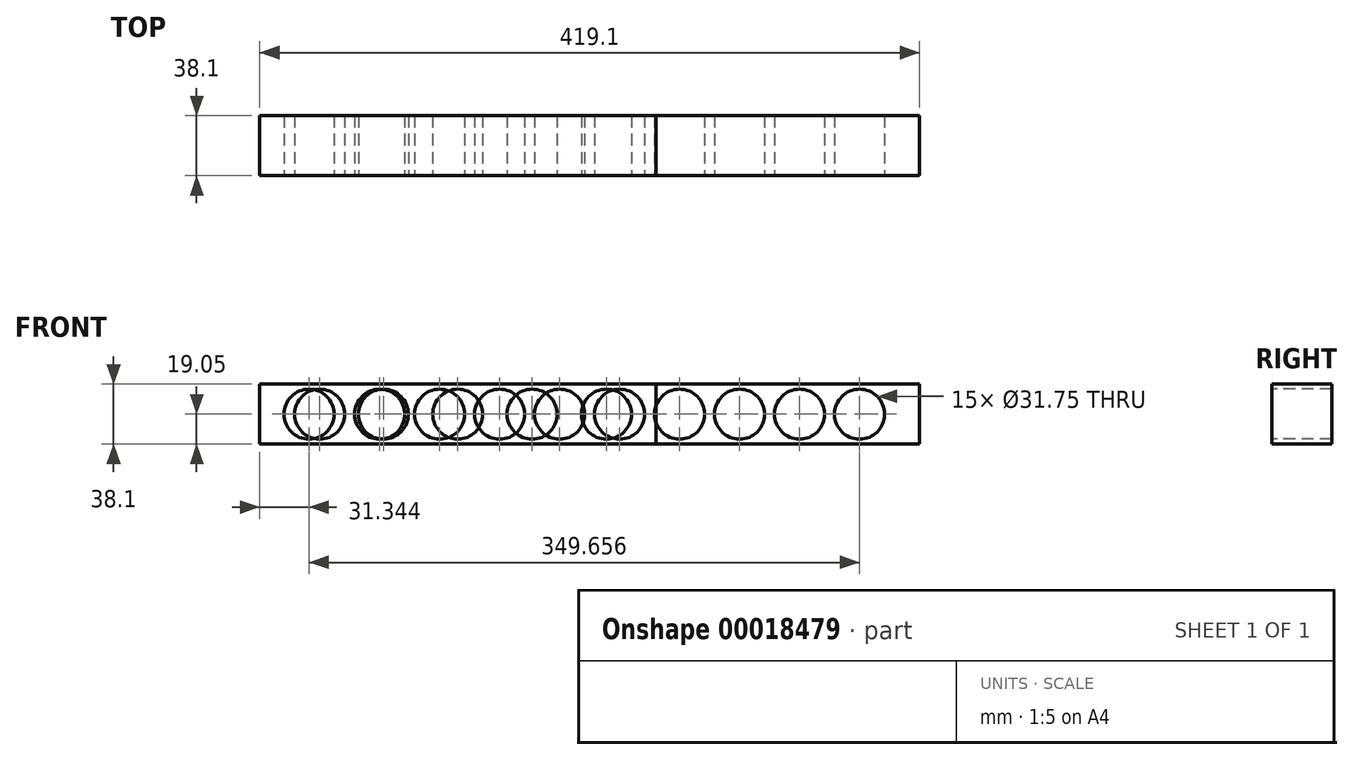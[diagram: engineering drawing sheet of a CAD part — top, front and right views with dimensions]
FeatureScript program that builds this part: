
annotation { "Feature Type Name" : "Feature", "Feature Type Description" : "" }
export const myFeature = defineFeature(function(context is Context, id is Id, definition is map)
    precondition{}
    {
        {
            var Q0;
            Q0=qCreatedBy(makeId("Right.planeOp"),FACE);
            var sketch = newSketch(context, id + "F0", { "sketchPlane" : qUnion([Q0])});
            skLineSegment(sketch, "E0.bottom", {"start": v(0, 0) * mm, "end": v(38.1, 0) * mm});
            skLineSegment(sketch, "E0.top", {"start": v(0, 38.1) * mm, "end": v(38.1, 38.1) * mm});
            skLineSegment(sketch, "E0.left", {"start": v(0, 0) * mm, "end": v(0, 38.1) * mm});
            skLineSegment(sketch, "E0.right", {"start": v(38.1, 0) * mm, "end": v(38.1, 38.1) * mm});
            skSolve(sketch);
        }
        {
            var Q0;
            Q0=makeQuery(id+"F0.imprint","IMPRINT",FACE,{"disambiguationData":[TD([[makeQuery(id+"F0.imprint","IMPRINT",EDGE,{"derivedFrom":sQuery(id+"F0.wireOp",EDGE,"E0.bottom")}),1.0]])]});
            extrude(context, id + "F1", {"entities" : qUnion([Q0]), "depth" : 419.1 * mm});
        }
        {
            var Q0;
            Q0=makeQuery(id+"F1.opExtrude","SWEPT_FACE",FACE,{"disambiguationData":[OSD([sQuery(id+"F0.wireOp",EDGE,"E0.left")])]});
            var sketch = newSketch(context, id + "F2", { "sketchPlane" : qUnion([Q0])});
            skPoint(sketch, "E1", {"position": v(38.1, 19.05) * mm});
            skPoint(sketch, "E2.1.0.0", {"position": v(76.2, 19.05) * mm});
            skPoint(sketch, "E2.2.0.0", {"position": v(114.3, 19.05) * mm});
            skPoint(sketch, "E2.3.0.0", {"position": v(152.4, 19.05) * mm});
            skPoint(sketch, "E2.4.0.0", {"position": v(190.5, 19.05) * mm});
            skPoint(sketch, "E2.5.0.0", {"position": v(228.6, 19.05) * mm});
            skPoint(sketch, "E2.6.0.0", {"position": v(266.7, 19.05) * mm});
            skPoint(sketch, "E2.7.0.0", {"position": v(304.8, 19.05) * mm});
            skPoint(sketch, "E2.8.0.0", {"position": v(342.9, 19.05) * mm});
            skPoint(sketch, "E2.9.0.0", {"position": v(381, 19.05) * mm});
            skLineSegment(sketch, "E2.direction1", {"start": v(38.1, 19.05) * mm, "end": v(76.2, 19.05) * mm, "construction": true});
            skSolve(sketch);
        }
        {
            var Q0;
            Q0=sQuery(id+"F2.wireOp",VERTEX,"E1");
            var Q1;
            Q1=sQuery(id+"F2.wireOp",VERTEX,"E2.1.0.0");
            var Q2;
            Q2=sQuery(id+"F2.wireOp",VERTEX,"E2.2.0.0");
            var Q3;
            Q3=sQuery(id+"F2.wireOp",VERTEX,"E2.3.0.0");
            var Q4;
            Q4=sQuery(id+"F2.wireOp",VERTEX,"E2.4.0.0");
            var Q5;
            Q5=sQuery(id+"F2.wireOp",VERTEX,"E2.5.0.0");
            var Q6;
            Q6=sQuery(id+"F2.wireOp",VERTEX,"E2.6.0.0");
            var Q7;
            Q7=sQuery(id+"F2.wireOp",VERTEX,"E2.7.0.0");
            var Q8;
            Q8=sQuery(id+"F2.wireOp",VERTEX,"E2.8.0.0");
            var Q9;
            Q9=sQuery(id+"F2.wireOp",VERTEX,"E2.9.0.0");
            var Q10;
            Q10=makeQuery(id+"F1.opExtrude","SWEPT_BODY",BODY,{"disambiguationData":[OSD([sQuery(id+"F0.wireOp",EDGE,"E0.bottom"),sQuery(id+"F0.wireOp",EDGE,"E0.top"),sQuery(id+"F0.wireOp",EDGE,"E0.left"),sQuery(id+"F0.wireOp",EDGE,"E0.right")])]});
            hole(context, id + "F3", {"style" : HoleStyle.SIMPLE, "holeDiameter" : 31.75 * mm, "endStyle" : HoleEndStyle.THROUGH, "locations" : qUnion([Q0, Q1, Q2, Q3, Q4, Q5, Q6, Q7, Q8, Q9]), "scope" : qUnion([Q10])});
        }
        {
            var Q0;
            Q0 = qSketchRegion(id + "F0", true);
            extrude(context, id + "F4", {"entities" : qUnion([Q0]), "depth" : 251.61 * mm});
        }
        {
            var Q0;
            Q0=makeQuery(id+"F4.opExtrude","SWEPT_FACE",FACE,{"disambiguationData":[OSD([sQuery(id+"F0.wireOp",EDGE,"E0.left")])]});
            var sketch = newSketch(context, id + "F5", { "sketchPlane" : qUnion([Q0])});
            skPoint(sketch, "E3", {"position": v(31.34, 19.05) * mm});
            skPoint(sketch, "E4.1.0.0", {"position": v(78.56, 19.05) * mm});
            skPoint(sketch, "E4.2.0.0", {"position": v(125.78, 19.05) * mm});
            skPoint(sketch, "E4.3.0.0", {"position": v(173, 19.05) * mm});
            skPoint(sketch, "E4.4.0.0", {"position": v(220.22, 19.05) * mm});
            skLineSegment(sketch, "E4.direction1", {"start": v(31.34, 19.05) * mm, "end": v(78.56, 19.05) * mm, "construction": true});
            skSolve(sketch);
        }
        {
            var Q0;
            Q0=sQuery(id+"F5.wireOp",VERTEX,"E3");
            var Q1;
            Q1=sQuery(id+"F5.wireOp",VERTEX,"E4.1.0.0");
            var Q2;
            Q2=sQuery(id+"F5.wireOp",VERTEX,"E4.2.0.0");
            var Q3;
            Q3=sQuery(id+"F5.wireOp",VERTEX,"E4.3.0.0");
            var Q4;
            Q4=sQuery(id+"F5.wireOp",VERTEX,"E4.4.0.0");
            var Q5;
            Q5=makeQuery(id+"F4.opExtrude","SWEPT_BODY",BODY,{"disambiguationData":[OSD([sQuery(id+"F0.wireOp",EDGE,"E0.bottom"),sQuery(id+"F0.wireOp",EDGE,"E0.top"),sQuery(id+"F0.wireOp",EDGE,"E0.left"),sQuery(id+"F0.wireOp",EDGE,"E0.right")])]});
            hole(context, id + "F6", {"style" : HoleStyle.SIMPLE, "holeDiameter" : 31.75 * mm, "endStyle" : HoleEndStyle.THROUGH, "locations" : qUnion([Q0, Q1, Q2, Q3, Q4]), "scope" : qUnion([Q5])});
        }
    });
